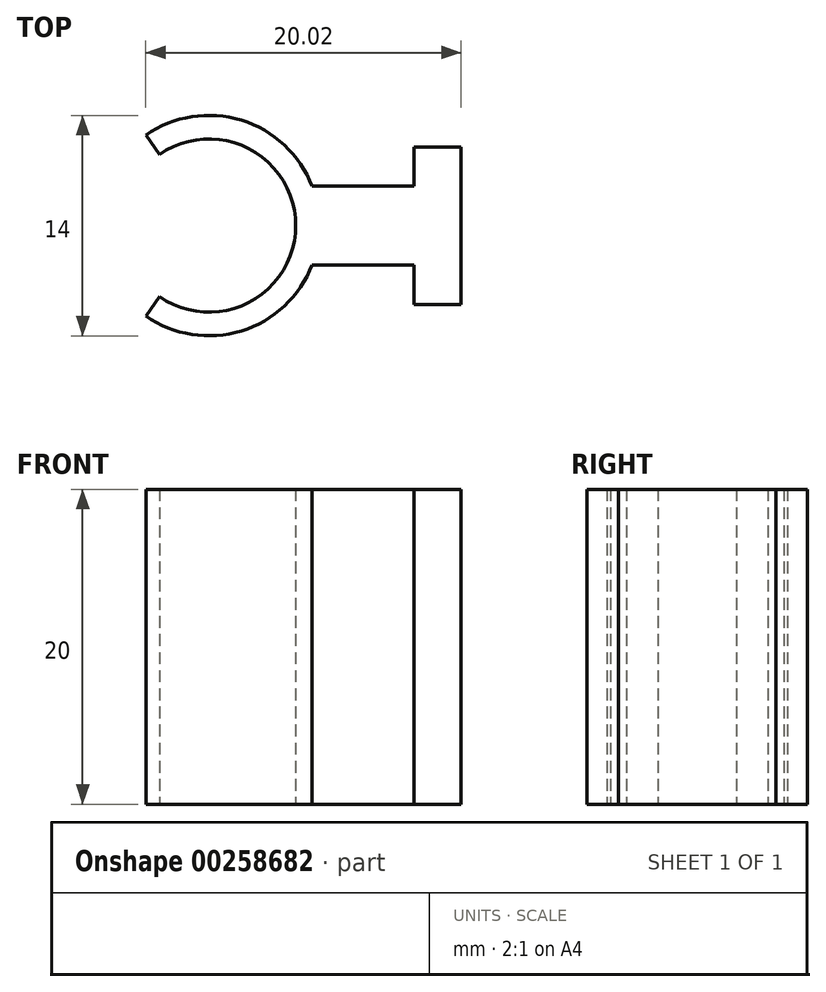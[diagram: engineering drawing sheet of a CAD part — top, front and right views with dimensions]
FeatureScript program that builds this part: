
annotation { "Feature Type Name" : "Feature", "Feature Type Description" : "" }
export const myFeature = defineFeature(function(context is Context, id is Id, definition is map)
    precondition{}
    {
        {
            var Q0;
            Q0=qCreatedBy(makeId("Top.planeOp"),FACE);
            var sketch = newSketch(context, id + "F0", { "sketchPlane" : qUnion([Q0])});
            skArc(sketch, "E0", {"start": v(-3.15, -4.5) * mm, "mid": v(5.5, 0) * mm, "end": v(-3.15, 4.5) * mm});
            skArc(sketch, "E1.0", {"start": v(6.54, 2.5) * mm, "mid": v(2.05, 6.7) * mm, "end": v(-4.02, 5.73) * mm});
            skLineSegment(sketch, "E2", {"start": v(6.54, 2.5) * mm, "end": v(13, 2.5) * mm});
            skLineSegment(sketch, "E3.MirrorCS", {"start": v(6.54, -2.5) * mm, "end": v(13, -2.5) * mm});
            skLineSegment(sketch, "E4", {"start": v(13, 2.5) * mm, "end": v(13, 5) * mm});
            skLineSegment(sketch, "E5", {"start": v(13, 5) * mm, "end": v(16, 5) * mm});
            skLineSegment(sketch, "E6", {"start": v(16, 5) * mm, "end": v(16, -5) * mm});
            skLineSegment(sketch, "E7.MirrorCS", {"start": v(13, -5) * mm, "end": v(16, -5) * mm});
            skLineSegment(sketch, "E8.MirrorCS", {"start": v(13, -2.5) * mm, "end": v(13, -5) * mm});
            skLineSegment(sketch, "E9", {"start": v(-3.15, 4.5) * mm, "end": v(-4.02, 5.73) * mm});
            skLineSegment(sketch, "E10.MirrorCS", {"start": v(-3.15, -4.5) * mm, "end": v(-4.02, -5.73) * mm});
            skPoint(sketch, "E11.orphan", {"position": v(-6.27, 8.96) * mm});
            skArc(sketch, "E12.trimOffspring", {"start": v(-4.02, -5.73) * mm, "mid": v(2.05, -6.7) * mm, "end": v(6.54, -2.5) * mm});
            skPoint(sketch, "E13.orphan", {"position": v(-6.27, -8.96) * mm});
            skSolve(sketch);
        }
        {
            var Q0;
            Q0 = qSketchRegion(id + "F0", true);
            extrude(context, id + "F1", {"entities" : qUnion([Q0]), "depth" : 20 * mm});
        }
    });
